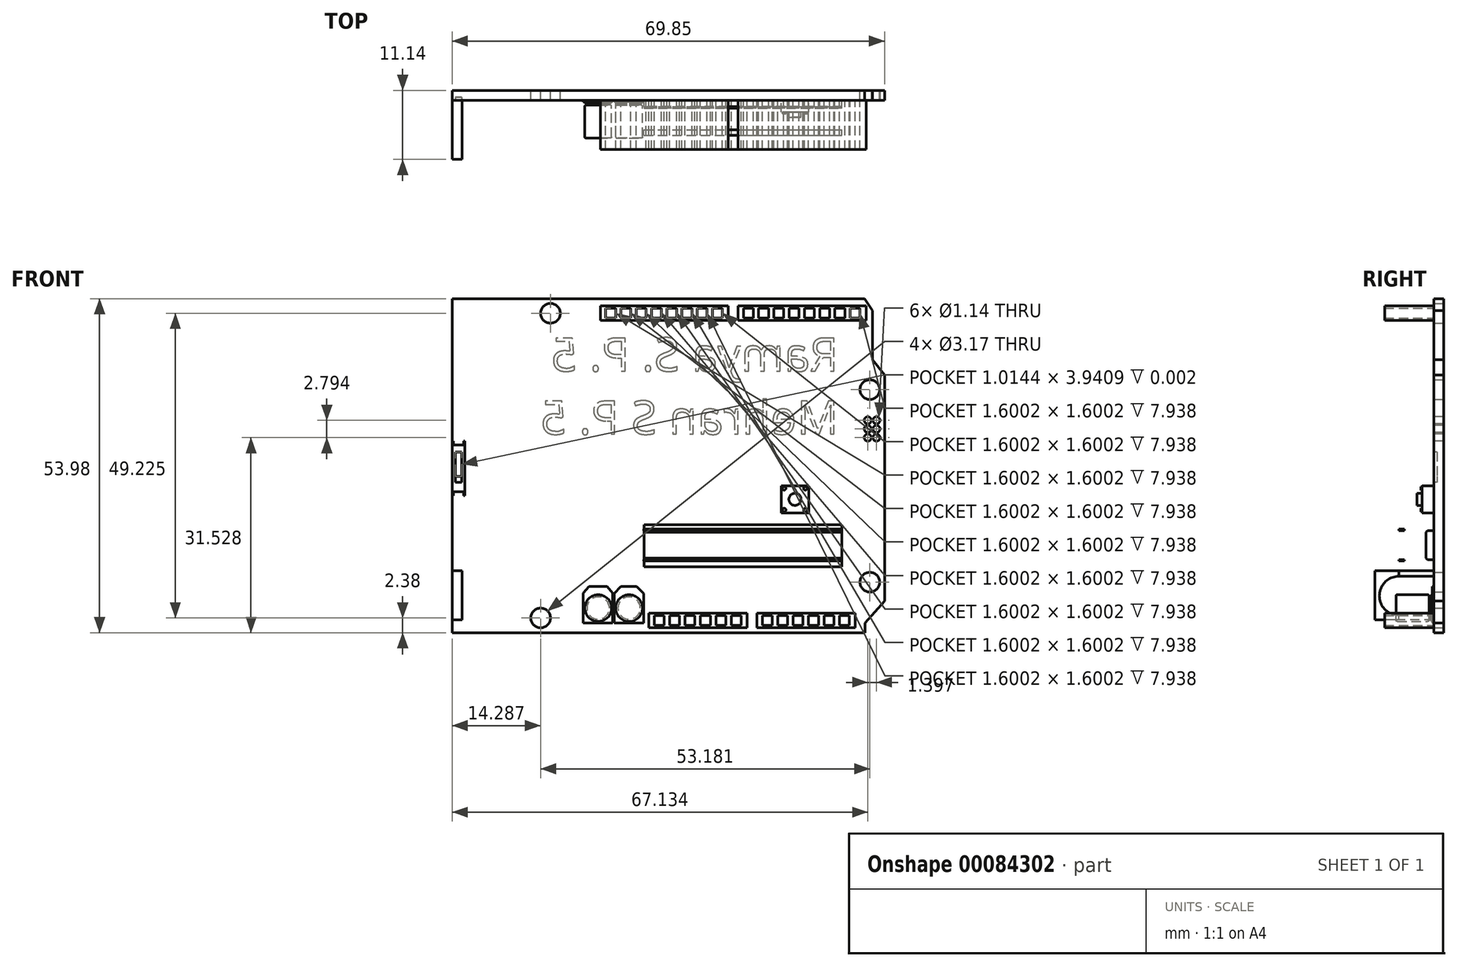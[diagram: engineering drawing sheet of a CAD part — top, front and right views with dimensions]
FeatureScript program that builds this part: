
annotation { "Feature Type Name" : "Feature", "Feature Type Description" : "" }
export const myFeature = defineFeature(function(context is Context, id is Id, definition is map)
    precondition{}
    {
        {
            var Q0;
            Q0=qCreatedBy(makeId("Front.planeOp"),FACE);
            var sketch = newSketch(context, id + "F0", { "sketchPlane" : qUnion([Q0])});
            skLineSegment(sketch, "E0.bottom", {"start": v(0, 0) * mm, "end": v(69.85, 0) * mm});
            skLineSegment(sketch, "E0.top", {"start": v(0, -53.97) * mm, "end": v(69.85, -53.97) * mm});
            skLineSegment(sketch, "E0.left", {"start": v(0, 0) * mm, "end": v(0, -53.97) * mm});
            skLineSegment(sketch, "E0.right", {"start": v(69.85, 0) * mm, "end": v(69.85, -53.97) * mm});
            skLineSegment(sketch, "E1", {"start": v(66.68, -53.97) * mm, "end": v(66.68, -52.39) * mm});
            skLineSegment(sketch, "E2", {"start": v(66.68, -52.39) * mm, "end": v(69.85, -48.84) * mm});
            skLineSegment(sketch, "E3", {"start": v(69.85, -12.33) * mm, "end": v(67.87, -9.84) * mm});
            skLineSegment(sketch, "E4", {"start": v(67.87, -9.84) * mm, "end": v(67.87, -1.9) * mm});
            skLineSegment(sketch, "E5", {"start": v(67.87, -1.9) * mm, "end": v(66.6, 0) * mm});
            skCircle(sketch, "E6", {"center": v(67.47, -14.7) * mm, "radius": 1.59 * mm});
            skCircle(sketch, "E7", {"center": v(67.47, -45.82) * mm, "radius": 1.59 * mm});
            skCircle(sketch, "E8", {"center": v(15.88, -2.37) * mm, "radius": 1.59 * mm});
            skCircle(sketch, "E9", {"center": v(14.29, -51.6) * mm, "radius": 1.59 * mm});
            skSolve(sketch);
        }
        {
            var Q0;
            {var subQ3=sQuery(id+"F0.wireOp",EDGE,"E0.left");Q0=makeQuery(id+"F0.imprint","IMPRINT",FACE,{"disambiguationData":[TD([[makeQuery(id+"F0.imprint","IMPRINT",EDGE,{"derivedFrom":subQ3}),1.0]])]});}
            extrude(context, id + "F1", {"entities" : qUnion([Q0]), "depth" : 1.59 * mm});
        }
        {
            var Q0;
            Q0=makeQuery(id+"F1.opExtrude","CAP_FACE",FACE,{"disambiguationData":[OSD([sQuery(id+"F0.wireOp",EDGE,"E0.bottom"),sQuery(id+"F0.wireOp",EDGE,"E0.top"),sQuery(id+"F0.wireOp",EDGE,"E0.left"),sQuery(id+"F0.wireOp",EDGE,"E0.right"),sQuery(id+"F0.wireOp",EDGE,"E1"),sQuery(id+"F0.wireOp",EDGE,"E2"),sQuery(id+"F0.wireOp",EDGE,"E3"),sQuery(id+"F0.wireOp",EDGE,"E4"),sQuery(id+"F0.wireOp",EDGE,"E5"),sQuery(id+"F0.wireOp",EDGE,"E6"),sQuery(id+"F0.wireOp",EDGE,"E7"),sQuery(id+"F0.wireOp",EDGE,"E8"),sQuery(id+"F0.wireOp",EDGE,"E9")])],"isStart":false});
            var sketch = newSketch(context, id + "F2", { "sketchPlane" : qUnion([Q0])});
            skLineSegment(sketch, "E10.bottom", {"start": v(65.09, -53.19) * mm, "end": v(49.21, -53.19) * mm});
            skLineSegment(sketch, "E10.top", {"start": v(65.09, -50.81) * mm, "end": v(49.21, -50.81) * mm});
            skLineSegment(sketch, "E10.left", {"start": v(65.09, -53.19) * mm, "end": v(65.09, -50.81) * mm});
            skLineSegment(sketch, "E10.right", {"start": v(49.21, -53.19) * mm, "end": v(49.21, -50.81) * mm});
            skLineSegment(sketch, "E11.bottom", {"start": v(47.63, -53.19) * mm, "end": v(31.75, -53.19) * mm});
            skLineSegment(sketch, "E11.top", {"start": v(47.63, -50.8) * mm, "end": v(31.75, -50.8) * mm});
            skLineSegment(sketch, "E11.left", {"start": v(47.63, -53.19) * mm, "end": v(47.63, -50.8) * mm});
            skLineSegment(sketch, "E11.right", {"start": v(31.75, -53.19) * mm, "end": v(31.75, -50.8) * mm});
            skLineSegment(sketch, "E12.bottom", {"start": v(46.2, -1.14) * mm, "end": v(66.86, -1.14) * mm});
            skLineSegment(sketch, "E12.top", {"start": v(46.2, -3.52) * mm, "end": v(66.86, -3.52) * mm});
            skLineSegment(sketch, "E12.left", {"start": v(46.2, -1.14) * mm, "end": v(46.2, -3.52) * mm});
            skLineSegment(sketch, "E12.right", {"start": v(66.86, -1.14) * mm, "end": v(66.86, -3.52) * mm});
            skLineSegment(sketch, "E13.bottom", {"start": v(44.62, -1.14) * mm, "end": v(23.97, -1.14) * mm});
            skLineSegment(sketch, "E13.top", {"start": v(44.62, -3.52) * mm, "end": v(23.97, -3.52) * mm});
            skLineSegment(sketch, "E13.left", {"start": v(44.62, -1.14) * mm, "end": v(44.62, -3.52) * mm});
            skLineSegment(sketch, "E13.right", {"start": v(23.97, -1.14) * mm, "end": v(23.97, -3.52) * mm});
            skLineSegment(sketch, "E14.bottom", {"start": v(24.8, -1.54) * mm, "end": v(26.4, -1.54) * mm});
            skLineSegment(sketch, "E14.top", {"start": v(24.8, -3.14) * mm, "end": v(26.4, -3.14) * mm});
            skLineSegment(sketch, "E14.left", {"start": v(24.8, -1.54) * mm, "end": v(24.8, -3.14) * mm});
            skLineSegment(sketch, "E14.right", {"start": v(26.4, -1.54) * mm, "end": v(26.4, -3.14) * mm});
            skLineSegment(sketch, "E15.bottom", {"start": v(27.27, -1.54) * mm, "end": v(28.87, -1.54) * mm});
            skLineSegment(sketch, "E15.top", {"start": v(27.27, -3.14) * mm, "end": v(28.87, -3.14) * mm});
            skLineSegment(sketch, "E15.left", {"start": v(27.27, -1.54) * mm, "end": v(27.27, -3.14) * mm});
            skLineSegment(sketch, "E15.right", {"start": v(28.87, -1.54) * mm, "end": v(28.87, -3.14) * mm});
            skLineSegment(sketch, "E16.bottom", {"start": v(29.73, -1.54) * mm, "end": v(31.33, -1.54) * mm});
            skLineSegment(sketch, "E16.top", {"start": v(29.73, -3.14) * mm, "end": v(31.33, -3.14) * mm});
            skLineSegment(sketch, "E16.left", {"start": v(29.73, -1.54) * mm, "end": v(29.73, -3.14) * mm});
            skLineSegment(sketch, "E16.right", {"start": v(31.33, -1.54) * mm, "end": v(31.33, -3.14) * mm});
            skLineSegment(sketch, "E17.bottom", {"start": v(32.2, -1.54) * mm, "end": v(33.8, -1.54) * mm});
            skLineSegment(sketch, "E17.top", {"start": v(32.2, -3.14) * mm, "end": v(33.8, -3.14) * mm});
            skLineSegment(sketch, "E17.left", {"start": v(32.2, -1.54) * mm, "end": v(32.2, -3.14) * mm});
            skLineSegment(sketch, "E17.right", {"start": v(33.8, -1.54) * mm, "end": v(33.8, -3.14) * mm});
            skLineSegment(sketch, "E18.bottom", {"start": v(34.66, -1.54) * mm, "end": v(36.26, -1.54) * mm});
            skLineSegment(sketch, "E18.top", {"start": v(34.66, -3.14) * mm, "end": v(36.26, -3.14) * mm});
            skLineSegment(sketch, "E18.left", {"start": v(34.66, -1.54) * mm, "end": v(34.66, -3.14) * mm});
            skLineSegment(sketch, "E18.right", {"start": v(36.26, -1.54) * mm, "end": v(36.26, -3.14) * mm});
            skLineSegment(sketch, "E19.bottom", {"start": v(37.12, -1.54) * mm, "end": v(38.72, -1.54) * mm});
            skLineSegment(sketch, "E19.top", {"start": v(37.12, -3.14) * mm, "end": v(38.72, -3.14) * mm});
            skLineSegment(sketch, "E19.left", {"start": v(37.12, -1.54) * mm, "end": v(37.12, -3.14) * mm});
            skLineSegment(sketch, "E19.right", {"start": v(38.72, -1.54) * mm, "end": v(38.72, -3.14) * mm});
            skLineSegment(sketch, "E20.bottom", {"start": v(39.59, -1.54) * mm, "end": v(41.19, -1.54) * mm});
            skLineSegment(sketch, "E20.top", {"start": v(39.59, -3.14) * mm, "end": v(41.19, -3.14) * mm});
            skLineSegment(sketch, "E20.left", {"start": v(39.59, -1.54) * mm, "end": v(39.59, -3.14) * mm});
            skLineSegment(sketch, "E20.right", {"start": v(41.19, -1.54) * mm, "end": v(41.19, -3.14) * mm});
            skLineSegment(sketch, "E21.bottom", {"start": v(42.05, -1.54) * mm, "end": v(43.65, -1.54) * mm});
            skLineSegment(sketch, "E21.top", {"start": v(42.05, -3.14) * mm, "end": v(43.65, -3.14) * mm});
            skLineSegment(sketch, "E21.left", {"start": v(42.05, -1.54) * mm, "end": v(42.05, -3.14) * mm});
            skLineSegment(sketch, "E21.right", {"start": v(43.65, -1.54) * mm, "end": v(43.65, -3.14) * mm});
            skLineSegment(sketch, "E22.bottom", {"start": v(47.04, -1.55) * mm, "end": v(48.64, -1.55) * mm});
            skLineSegment(sketch, "E22.top", {"start": v(47.04, -3.15) * mm, "end": v(48.64, -3.15) * mm});
            skLineSegment(sketch, "E22.left", {"start": v(47.04, -1.55) * mm, "end": v(47.04, -3.15) * mm});
            skLineSegment(sketch, "E22.right", {"start": v(48.64, -1.55) * mm, "end": v(48.64, -3.15) * mm});
            skPoint(sketch, "E23.firstSnap0", {"position": v(47.84, -1.55) * mm});
            skLineSegment(sketch, "E23.bottom", {"start": v(49.5, -1.55) * mm, "end": v(51.1, -1.55) * mm});
            skLineSegment(sketch, "E23.top", {"start": v(49.5, -3.15) * mm, "end": v(51.1, -3.15) * mm});
            skLineSegment(sketch, "E23.left", {"start": v(49.5, -1.55) * mm, "end": v(49.5, -3.15) * mm});
            skLineSegment(sketch, "E23.right", {"start": v(51.1, -1.55) * mm, "end": v(51.1, -3.15) * mm});
            skLineSegment(sketch, "E24.bottom", {"start": v(51.97, -1.55) * mm, "end": v(53.57, -1.55) * mm});
            skLineSegment(sketch, "E24.top", {"start": v(51.97, -3.15) * mm, "end": v(53.57, -3.15) * mm});
            skLineSegment(sketch, "E24.left", {"start": v(51.97, -1.55) * mm, "end": v(51.97, -3.15) * mm});
            skLineSegment(sketch, "E24.right", {"start": v(53.57, -1.55) * mm, "end": v(53.57, -3.15) * mm});
            skLineSegment(sketch, "E25.bottom", {"start": v(54.43, -1.55) * mm, "end": v(56.04, -1.55) * mm});
            skLineSegment(sketch, "E25.top", {"start": v(54.43, -3.15) * mm, "end": v(56.04, -3.15) * mm});
            skLineSegment(sketch, "E25.left", {"start": v(54.43, -1.55) * mm, "end": v(54.43, -3.15) * mm});
            skLineSegment(sketch, "E25.right", {"start": v(56.04, -1.55) * mm, "end": v(56.04, -3.15) * mm});
            skLineSegment(sketch, "E26.bottom", {"start": v(56.9, -1.55) * mm, "end": v(58.5, -1.55) * mm});
            skLineSegment(sketch, "E26.top", {"start": v(56.9, -3.15) * mm, "end": v(58.5, -3.15) * mm});
            skLineSegment(sketch, "E26.left", {"start": v(56.9, -1.55) * mm, "end": v(56.9, -3.15) * mm});
            skLineSegment(sketch, "E26.right", {"start": v(58.5, -1.55) * mm, "end": v(58.5, -3.15) * mm});
            skLineSegment(sketch, "E27.bottom", {"start": v(59.36, -1.55) * mm, "end": v(60.96, -1.55) * mm});
            skLineSegment(sketch, "E27.top", {"start": v(59.36, -3.15) * mm, "end": v(60.96, -3.15) * mm});
            skLineSegment(sketch, "E27.left", {"start": v(59.36, -1.55) * mm, "end": v(59.36, -3.15) * mm});
            skLineSegment(sketch, "E27.right", {"start": v(60.96, -1.55) * mm, "end": v(60.96, -3.15) * mm});
            skLineSegment(sketch, "E28.bottom", {"start": v(61.83, -1.55) * mm, "end": v(63.43, -1.55) * mm});
            skLineSegment(sketch, "E28.top", {"start": v(61.83, -3.15) * mm, "end": v(63.43, -3.15) * mm});
            skLineSegment(sketch, "E28.left", {"start": v(61.83, -1.55) * mm, "end": v(61.83, -3.15) * mm});
            skLineSegment(sketch, "E28.right", {"start": v(63.43, -1.55) * mm, "end": v(63.43, -3.15) * mm});
            skLineSegment(sketch, "E29.bottom", {"start": v(64.3, -1.55) * mm, "end": v(65.9, -1.55) * mm});
            skLineSegment(sketch, "E29.top", {"start": v(64.3, -3.15) * mm, "end": v(65.9, -3.15) * mm});
            skLineSegment(sketch, "E29.left", {"start": v(64.3, -1.55) * mm, "end": v(64.3, -3.15) * mm});
            skLineSegment(sketch, "E29.right", {"start": v(65.9, -1.55) * mm, "end": v(65.9, -3.15) * mm});
            skLineSegment(sketch, "E30.bottom", {"start": v(32.64, -51.2) * mm, "end": v(34.24, -51.2) * mm});
            skLineSegment(sketch, "E30.top", {"start": v(32.64, -52.8) * mm, "end": v(34.24, -52.8) * mm});
            skLineSegment(sketch, "E30.left", {"start": v(32.64, -51.2) * mm, "end": v(32.64, -52.8) * mm});
            skLineSegment(sketch, "E30.right", {"start": v(34.24, -51.2) * mm, "end": v(34.24, -52.8) * mm});
            skLineSegment(sketch, "E31.bottom", {"start": v(35.13, -51.2) * mm, "end": v(36.73, -51.2) * mm});
            skLineSegment(sketch, "E31.top", {"start": v(35.13, -52.8) * mm, "end": v(36.73, -52.8) * mm});
            skLineSegment(sketch, "E31.left", {"start": v(35.13, -51.2) * mm, "end": v(35.13, -52.8) * mm});
            skLineSegment(sketch, "E31.right", {"start": v(36.73, -51.2) * mm, "end": v(36.73, -52.8) * mm});
            skLineSegment(sketch, "E32.bottom", {"start": v(37.62, -51.2) * mm, "end": v(39.22, -51.2) * mm});
            skLineSegment(sketch, "E32.top", {"start": v(37.62, -52.8) * mm, "end": v(39.22, -52.8) * mm});
            skLineSegment(sketch, "E32.left", {"start": v(37.62, -51.2) * mm, "end": v(37.62, -52.8) * mm});
            skLineSegment(sketch, "E32.right", {"start": v(39.22, -51.2) * mm, "end": v(39.22, -52.8) * mm});
            skLineSegment(sketch, "E33.bottom", {"start": v(40.1, -51.2) * mm, "end": v(41.7, -51.2) * mm});
            skLineSegment(sketch, "E33.top", {"start": v(40.1, -52.8) * mm, "end": v(41.7, -52.8) * mm});
            skLineSegment(sketch, "E33.left", {"start": v(40.1, -51.2) * mm, "end": v(40.1, -52.8) * mm});
            skLineSegment(sketch, "E33.right", {"start": v(41.7, -51.2) * mm, "end": v(41.7, -52.8) * mm});
            skLineSegment(sketch, "E34.bottom", {"start": v(42.6, -51.2) * mm, "end": v(44.2, -51.2) * mm});
            skLineSegment(sketch, "E34.top", {"start": v(42.6, -52.8) * mm, "end": v(44.2, -52.8) * mm});
            skLineSegment(sketch, "E34.left", {"start": v(42.6, -51.2) * mm, "end": v(42.6, -52.8) * mm});
            skLineSegment(sketch, "E34.right", {"start": v(44.2, -51.2) * mm, "end": v(44.2, -52.8) * mm});
            skLineSegment(sketch, "E35.bottom", {"start": v(45.09, -51.2) * mm, "end": v(46.69, -51.2) * mm});
            skLineSegment(sketch, "E35.top", {"start": v(45.09, -52.8) * mm, "end": v(46.69, -52.8) * mm});
            skLineSegment(sketch, "E35.left", {"start": v(45.09, -51.2) * mm, "end": v(45.09, -52.8) * mm});
            skLineSegment(sketch, "E35.right", {"start": v(46.69, -51.2) * mm, "end": v(46.69, -52.8) * mm});
            skLineSegment(sketch, "E36.bottom", {"start": v(50.1, -51.22) * mm, "end": v(51.7, -51.22) * mm});
            skLineSegment(sketch, "E36.top", {"start": v(50.1, -52.82) * mm, "end": v(51.7, -52.82) * mm});
            skLineSegment(sketch, "E36.left", {"start": v(50.1, -51.22) * mm, "end": v(50.1, -52.82) * mm});
            skLineSegment(sketch, "E36.right", {"start": v(51.7, -51.22) * mm, "end": v(51.7, -52.82) * mm});
            skLineSegment(sketch, "E37.bottom", {"start": v(52.6, -51.22) * mm, "end": v(54.2, -51.22) * mm});
            skLineSegment(sketch, "E37.top", {"start": v(52.6, -52.82) * mm, "end": v(54.2, -52.82) * mm});
            skLineSegment(sketch, "E37.left", {"start": v(52.6, -51.22) * mm, "end": v(52.6, -52.82) * mm});
            skLineSegment(sketch, "E37.right", {"start": v(54.2, -51.22) * mm, "end": v(54.2, -52.82) * mm});
            skLineSegment(sketch, "E38.bottom", {"start": v(55.08, -51.22) * mm, "end": v(56.68, -51.22) * mm});
            skLineSegment(sketch, "E38.top", {"start": v(55.08, -52.82) * mm, "end": v(56.68, -52.82) * mm});
            skLineSegment(sketch, "E38.left", {"start": v(55.08, -51.22) * mm, "end": v(55.08, -52.82) * mm});
            skLineSegment(sketch, "E38.right", {"start": v(56.68, -51.22) * mm, "end": v(56.68, -52.82) * mm});
            skLineSegment(sketch, "E39.bottom", {"start": v(57.57, -51.22) * mm, "end": v(59.17, -51.22) * mm});
            skLineSegment(sketch, "E39.top", {"start": v(57.57, -52.82) * mm, "end": v(59.17, -52.82) * mm});
            skLineSegment(sketch, "E39.left", {"start": v(57.57, -51.22) * mm, "end": v(57.57, -52.82) * mm});
            skLineSegment(sketch, "E39.right", {"start": v(59.17, -51.22) * mm, "end": v(59.17, -52.82) * mm});
            skLineSegment(sketch, "E40.bottom", {"start": v(60.06, -51.22) * mm, "end": v(61.66, -51.22) * mm});
            skLineSegment(sketch, "E40.top", {"start": v(60.06, -52.82) * mm, "end": v(61.66, -52.82) * mm});
            skLineSegment(sketch, "E40.left", {"start": v(60.06, -51.22) * mm, "end": v(60.06, -52.82) * mm});
            skLineSegment(sketch, "E40.right", {"start": v(61.66, -51.22) * mm, "end": v(61.66, -52.82) * mm});
            skLineSegment(sketch, "E41.bottom", {"start": v(62.55, -51.22) * mm, "end": v(64.15, -51.22) * mm});
            skLineSegment(sketch, "E41.top", {"start": v(62.55, -52.82) * mm, "end": v(64.15, -52.82) * mm});
            skLineSegment(sketch, "E41.left", {"start": v(62.55, -51.22) * mm, "end": v(62.55, -52.82) * mm});
            skLineSegment(sketch, "E41.right", {"start": v(64.15, -51.22) * mm, "end": v(64.15, -52.82) * mm});
            skSolve(sketch);
        }
        {
            var Q0;
            Q0 = qSketchRegion(id + "F2", true);
            extrude(context, id + "F3", {"entities" : qUnion([Q0]), "operationType" : NewBodyOperationType.ADD, "depth" : 7.94 * mm});
        }
        {
            var Q0;
            Q0=makeQuery(id+"F1.opExtrude","CAP_FACE",FACE,{"disambiguationData":[OSD([sQuery(id+"F0.wireOp",EDGE,"E0.bottom"),sQuery(id+"F0.wireOp",EDGE,"E0.top"),sQuery(id+"F0.wireOp",EDGE,"E0.left"),sQuery(id+"F0.wireOp",EDGE,"E0.right"),sQuery(id+"F0.wireOp",EDGE,"E1"),sQuery(id+"F0.wireOp",EDGE,"E2"),sQuery(id+"F0.wireOp",EDGE,"E3"),sQuery(id+"F0.wireOp",EDGE,"E4"),sQuery(id+"F0.wireOp",EDGE,"E5"),sQuery(id+"F0.wireOp",EDGE,"E6"),sQuery(id+"F0.wireOp",EDGE,"E7"),sQuery(id+"F0.wireOp",EDGE,"E8"),sQuery(id+"F0.wireOp",EDGE,"E9")])],"isStart":true});
            var sketch = newSketch(context, id + "F4", { "sketchPlane" : qUnion([Q0])});
            skText(sketch, "E42", { "text": "Ramya S. P. 5\nMehran S P. 5", "fontName": "OpenSans-Regular.ttf"});
            const initialGuessF4  = {"E42": [-0.06243, -0.0117, 1, 0, 0.0054]};
            skSetInitialGuess(sketch, initialGuessF4);
            skSolve(sketch);
        }
        {
            var Q0;
            Q0 = qSketchRegion(id + "F4", true);
            extrude(context, id + "F5", {"entities" : qUnion([Q0]), "operationType" : NewBodyOperationType.ADD, "depth" : 0.03 * mm});
        }
        {
            var Q0;
            {var subQ0=sQuery(id+"F0.wireOp",EDGE,"E0.left");var subQ1=sQuery(id+"F0.wireOp",EDGE,"E2");var subQ2=sQuery(id+"F0.wireOp",EDGE,"E0.top");var subQ3=sQuery(id+"F0.wireOp",EDGE,"E9");var subQ4=sQuery(id+"F0.wireOp",EDGE,"E8");var subQ5=sQuery(id+"F0.wireOp",EDGE,"E7");var subQ6=sQuery(id+"F0.wireOp",EDGE,"E0.right");var subQ7=sQuery(id+"F0.wireOp",EDGE,"E0.bottom");var subQ8=sQuery(id+"F0.wireOp",EDGE,"E5");var subQ9=sQuery(id+"F0.wireOp",EDGE,"E1");var subQ10=sQuery(id+"F0.wireOp",EDGE,"E3");var subQ11=sQuery(id+"F0.wireOp",EDGE,"E4");var subQ12=sQuery(id+"F0.wireOp",EDGE,"E6");Q0=makeQuery(id+"F3.boolean.opBoolean","SPLIT",FACE,{"disambiguationData":[TD([makeQuery(id+"F1.opExtrude","SWEPT_FACE",FACE,{"disambiguationData":[OSD([subQ7])]})])],"derivedFrom":makeQuery(id+"F1.opExtrude","CAP_FACE",FACE,{"disambiguationData":[OSD([subQ7,subQ2,subQ0,subQ6,subQ9,subQ1,subQ10,subQ11,subQ8,subQ12,subQ5,subQ4,subQ3])],"isStart":false})});}
            var sketch = newSketch(context, id + "F6", { "sketchPlane" : qUnion([Q0])});
            skLineSegment(sketch, "E43.bottom", {"start": v(62.97, -43.34) * mm, "end": v(30.97, -43.34) * mm});
            skLineSegment(sketch, "E43.top", {"start": v(62.97, -36.52) * mm, "end": v(30.97, -36.52) * mm});
            skLineSegment(sketch, "E43.left", {"start": v(62.97, -43.34) * mm, "end": v(62.97, -36.52) * mm});
            skLineSegment(sketch, "E43.right", {"start": v(30.97, -43.34) * mm, "end": v(30.97, -36.52) * mm});
            skSolve(sketch);
        }
        {
            var Q0;
            Q0=makeQuery(id+"F6.imprint","IMPRINT",FACE,{"disambiguationData":[TD([[makeQuery(id+"F6.imprint","IMPRINT",EDGE,{"derivedFrom":sQuery(id+"F6.wireOp",EDGE,"E43.bottom")}),-1.0]])]});
            extrude(context, id + "F7", {"entities" : qUnion([Q0]), "operationType" : NewBodyOperationType.ADD, "depth" : 3 / 406.4 * mm});
        }
        {
            var Q0;
            Q0=makeQuery(id+"F7.opExtrude","CAP_FACE",FACE,{"disambiguationData":[OSD([sQuery(id+"F6.wireOp",EDGE,"E43.bottom"),sQuery(id+"F6.wireOp",EDGE,"E43.top"),sQuery(id+"F6.wireOp",EDGE,"E43.left"),sQuery(id+"F6.wireOp",EDGE,"E43.right")])],"isStart":false});
            var sketch = newSketch(context, id + "F8", { "sketchPlane" : qUnion([Q0])});
            skLineSegment(sketch, "E44.bottom", {"start": v(30.97, -37.48) * mm, "end": v(62.97, -37.48) * mm});
            skLineSegment(sketch, "E44.top", {"start": v(30.97, -42.17) * mm, "end": v(62.97, -42.17) * mm});
            skLineSegment(sketch, "E44.left", {"start": v(30.97, -37.48) * mm, "end": v(30.97, -42.17) * mm});
            skLineSegment(sketch, "E44.right", {"start": v(62.97, -37.48) * mm, "end": v(62.97, -42.17) * mm});
            skLineSegment(sketch, "E45.bottom", {"start": v(30.97, -42.17) * mm, "end": v(32.14, -42.17) * mm});
            skLineSegment(sketch, "E45.top", {"start": v(30.97, -37.48) * mm, "end": v(32.14, -37.48) * mm});
            skLineSegment(sketch, "E45.left", {"start": v(30.97, -42.17) * mm, "end": v(30.97, -37.48) * mm});
            skLineSegment(sketch, "E45.right", {"start": v(32.14, -42.17) * mm, "end": v(32.14, -37.48) * mm});
            skLineSegment(sketch, "E46.bottom", {"start": v(32.14, -42.17) * mm, "end": v(33.34, -42.17) * mm});
            skLineSegment(sketch, "E46.top", {"start": v(32.14, -37.48) * mm, "end": v(33.34, -37.48) * mm});
            skLineSegment(sketch, "E46.right", {"start": v(33.34, -42.17) * mm, "end": v(33.34, -37.48) * mm});
            skLineSegment(sketch, "E47.bottom", {"start": v(33.34, -42.17) * mm, "end": v(34.54, -42.17) * mm});
            skLineSegment(sketch, "E47.top", {"start": v(33.34, -37.48) * mm, "end": v(34.54, -37.48) * mm});
            skLineSegment(sketch, "E47.right", {"start": v(34.54, -42.17) * mm, "end": v(34.54, -37.48) * mm});
            skLineSegment(sketch, "E48.bottom", {"start": v(34.54, -42.17) * mm, "end": v(35.6, -42.17) * mm});
            skLineSegment(sketch, "E48.top", {"start": v(34.54, -37.48) * mm, "end": v(35.6, -37.48) * mm});
            skLineSegment(sketch, "E48.right", {"start": v(35.6, -42.17) * mm, "end": v(35.6, -37.48) * mm});
            skLineSegment(sketch, "E49.bottom", {"start": v(35.6, -42.17) * mm, "end": v(36.68, -42.17) * mm});
            skLineSegment(sketch, "E49.top", {"start": v(35.6, -37.48) * mm, "end": v(36.68, -37.48) * mm});
            skLineSegment(sketch, "E49.right", {"start": v(36.68, -42.17) * mm, "end": v(36.68, -37.48) * mm});
            skLineSegment(sketch, "E50.bottom", {"start": v(36.68, -42.17) * mm, "end": v(37.75, -42.17) * mm});
            skLineSegment(sketch, "E50.top", {"start": v(36.68, -37.48) * mm, "end": v(37.75, -37.48) * mm});
            skLineSegment(sketch, "E50.right", {"start": v(37.75, -42.17) * mm, "end": v(37.75, -37.48) * mm});
            skLineSegment(sketch, "E51.bottom", {"start": v(37.75, -42.17) * mm, "end": v(37.75, -42.17) * mm});
            skLineSegment(sketch, "E51.top", {"start": v(37.75, -37.48) * mm, "end": v(37.75, -37.48) * mm});
            skLineSegment(sketch, "E52.bottom", {"start": v(37.75, -42.17) * mm, "end": v(39.09, -42.17) * mm});
            skLineSegment(sketch, "E52.top", {"start": v(37.75, -37.48) * mm, "end": v(39.09, -37.48) * mm});
            skLineSegment(sketch, "E52.right", {"start": v(39.09, -42.17) * mm, "end": v(39.09, -37.48) * mm});
            skLineSegment(sketch, "E53.bottom", {"start": v(39.09, -42.17) * mm, "end": v(40.3, -42.17) * mm});
            skLineSegment(sketch, "E53.top", {"start": v(39.09, -37.48) * mm, "end": v(40.3, -37.48) * mm});
            skLineSegment(sketch, "E53.right", {"start": v(40.3, -42.17) * mm, "end": v(40.3, -37.48) * mm});
            skLineSegment(sketch, "E54.bottom", {"start": v(40.3, -42.17) * mm, "end": v(41.63, -42.17) * mm});
            skLineSegment(sketch, "E54.top", {"start": v(40.3, -37.48) * mm, "end": v(41.63, -37.48) * mm});
            skLineSegment(sketch, "E54.right", {"start": v(41.63, -42.17) * mm, "end": v(41.63, -37.48) * mm});
            skLineSegment(sketch, "E55.bottom", {"start": v(41.63, -42.17) * mm, "end": v(42.83, -42.17) * mm});
            skLineSegment(sketch, "E55.top", {"start": v(41.63, -37.48) * mm, "end": v(42.83, -37.48) * mm});
            skLineSegment(sketch, "E55.right", {"start": v(42.83, -42.17) * mm, "end": v(42.83, -37.48) * mm});
            skLineSegment(sketch, "E56.bottom", {"start": v(42.83, -42.17) * mm, "end": v(44.04, -42.17) * mm});
            skLineSegment(sketch, "E56.top", {"start": v(42.83, -37.48) * mm, "end": v(44.04, -37.48) * mm});
            skLineSegment(sketch, "E56.right", {"start": v(44.04, -42.17) * mm, "end": v(44.04, -37.48) * mm});
            skLineSegment(sketch, "E57.bottom", {"start": v(44.04, -42.17) * mm, "end": v(45.23, -42.17) * mm});
            skLineSegment(sketch, "E57.top", {"start": v(44.04, -37.48) * mm, "end": v(45.23, -37.48) * mm});
            skLineSegment(sketch, "E57.right", {"start": v(45.23, -42.17) * mm, "end": v(45.23, -37.48) * mm});
            skLineSegment(sketch, "E58.bottom", {"start": v(45.23, -42.17) * mm, "end": v(45.23, -42.17) * mm});
            skLineSegment(sketch, "E58.top", {"start": v(45.23, -37.48) * mm, "end": v(45.23, -37.48) * mm});
            skLineSegment(sketch, "E59.bottom", {"start": v(45.23, -42.17) * mm, "end": v(46.97, -42.17) * mm});
            skLineSegment(sketch, "E59.top", {"start": v(45.23, -37.48) * mm, "end": v(46.97, -37.48) * mm});
            skLineSegment(sketch, "E59.right", {"start": v(46.97, -42.17) * mm, "end": v(46.97, -37.48) * mm});
            skLineSegment(sketch, "E60.bottom", {"start": v(46.97, -42.17) * mm, "end": v(48.18, -42.17) * mm});
            skLineSegment(sketch, "E60.top", {"start": v(46.97, -37.48) * mm, "end": v(48.18, -37.48) * mm});
            skLineSegment(sketch, "E60.right", {"start": v(48.18, -42.17) * mm, "end": v(48.18, -37.48) * mm});
            skLineSegment(sketch, "E61.bottom", {"start": v(48.18, -42.17) * mm, "end": v(49.26, -42.17) * mm});
            skLineSegment(sketch, "E61.top", {"start": v(48.18, -37.48) * mm, "end": v(49.26, -37.48) * mm});
            skLineSegment(sketch, "E61.right", {"start": v(49.26, -42.17) * mm, "end": v(49.26, -37.48) * mm});
            skLineSegment(sketch, "E62.bottom", {"start": v(49.26, -42.17) * mm, "end": v(50.32, -42.17) * mm});
            skLineSegment(sketch, "E62.top", {"start": v(49.26, -37.48) * mm, "end": v(50.32, -37.48) * mm});
            skLineSegment(sketch, "E62.right", {"start": v(50.32, -42.17) * mm, "end": v(50.32, -37.48) * mm});
            skLineSegment(sketch, "E63.bottom", {"start": v(50.32, -42.17) * mm, "end": v(51.53, -42.17) * mm});
            skLineSegment(sketch, "E63.top", {"start": v(50.32, -37.48) * mm, "end": v(51.53, -37.48) * mm});
            skLineSegment(sketch, "E63.right", {"start": v(51.53, -42.17) * mm, "end": v(51.53, -37.48) * mm});
            skLineSegment(sketch, "E64.bottom", {"start": v(51.53, -42.17) * mm, "end": v(52.73, -42.17) * mm});
            skLineSegment(sketch, "E64.top", {"start": v(51.53, -37.48) * mm, "end": v(52.73, -37.48) * mm});
            skLineSegment(sketch, "E64.right", {"start": v(52.73, -42.17) * mm, "end": v(52.73, -37.48) * mm});
            skLineSegment(sketch, "E65.bottom", {"start": v(52.73, -42.17) * mm, "end": v(53.94, -42.17) * mm});
            skLineSegment(sketch, "E65.top", {"start": v(52.73, -37.48) * mm, "end": v(53.94, -37.48) * mm});
            skLineSegment(sketch, "E65.right", {"start": v(53.94, -42.17) * mm, "end": v(53.94, -37.48) * mm});
            skLineSegment(sketch, "E66.bottom", {"start": v(53.94, -42.17) * mm, "end": v(55.08, -42.17) * mm});
            skLineSegment(sketch, "E66.top", {"start": v(53.94, -37.48) * mm, "end": v(55.08, -37.48) * mm});
            skLineSegment(sketch, "E66.right", {"start": v(55.08, -42.17) * mm, "end": v(55.08, -37.48) * mm});
            skLineSegment(sketch, "E67.bottom", {"start": v(55.08, -42.17) * mm, "end": v(56.24, -42.17) * mm});
            skLineSegment(sketch, "E67.top", {"start": v(55.08, -37.48) * mm, "end": v(56.24, -37.48) * mm});
            skLineSegment(sketch, "E67.right", {"start": v(56.24, -42.17) * mm, "end": v(56.24, -37.48) * mm});
            skLineSegment(sketch, "E68.bottom", {"start": v(56.24, -42.17) * mm, "end": v(57.4, -42.17) * mm});
            skLineSegment(sketch, "E68.top", {"start": v(56.24, -37.48) * mm, "end": v(57.4, -37.48) * mm});
            skLineSegment(sketch, "E68.right", {"start": v(57.4, -42.17) * mm, "end": v(57.4, -37.48) * mm});
            skLineSegment(sketch, "E69.bottom", {"start": v(57.4, -42.17) * mm, "end": v(58.46, -42.17) * mm});
            skLineSegment(sketch, "E69.top", {"start": v(57.4, -37.48) * mm, "end": v(58.46, -37.48) * mm});
            skLineSegment(sketch, "E69.right", {"start": v(58.46, -42.17) * mm, "end": v(58.46, -37.48) * mm});
            skLineSegment(sketch, "E70.bottom", {"start": v(58.46, -42.17) * mm, "end": v(59.52, -42.17) * mm});
            skLineSegment(sketch, "E70.top", {"start": v(58.46, -37.48) * mm, "end": v(59.52, -37.48) * mm});
            skLineSegment(sketch, "E70.right", {"start": v(59.52, -42.17) * mm, "end": v(59.52, -37.48) * mm});
            skLineSegment(sketch, "E71.bottom", {"start": v(59.52, -42.17) * mm, "end": v(60.47, -42.17) * mm});
            skLineSegment(sketch, "E71.top", {"start": v(59.52, -37.48) * mm, "end": v(60.47, -37.48) * mm});
            skLineSegment(sketch, "E71.right", {"start": v(60.47, -42.17) * mm, "end": v(60.47, -37.48) * mm});
            skLineSegment(sketch, "E72.bottom", {"start": v(60.47, -42.17) * mm, "end": v(61.52, -42.17) * mm});
            skLineSegment(sketch, "E72.top", {"start": v(60.47, -37.48) * mm, "end": v(61.52, -37.48) * mm});
            skLineSegment(sketch, "E72.right", {"start": v(61.52, -42.17) * mm, "end": v(61.52, -37.48) * mm});
            skSolve(sketch);
        }
        {
            var Q0;
            Q0=makeQuery(id+"F8.imprint","IMPRINT",FACE,{"disambiguationData":[TD([[makeQuery(id+"F8.imprint","IMPRINT",EDGE,{"derivedFrom":sQuery(id+"F8.wireOp",EDGE,"E44.bottom")}),-1.0]])]});
            var Q1;
            Q1=makeQuery(id+"F8.imprint","IMPRINT",FACE,{"disambiguationData":[TD([[makeQuery(id+"F8.imprint","IMPRINT",EDGE,{"derivedFrom":sQuery(id+"F8.wireOp",EDGE,"E72.bottom")}),1.0]])]});
            var Q2;
            Q2=makeQuery(id+"F8.imprint","IMPRINT",FACE,{"disambiguationData":[TD([[makeQuery(id+"F8.imprint","IMPRINT",EDGE,{"derivedFrom":sQuery(id+"F8.wireOp",EDGE,"E71.bottom")}),1.0]])]});
            var Q3;
            Q3=makeQuery(id+"F8.imprint","IMPRINT",FACE,{"disambiguationData":[TD([[makeQuery(id+"F8.imprint","IMPRINT",EDGE,{"derivedFrom":sQuery(id+"F8.wireOp",EDGE,"E70.bottom")}),1.0]])]});
            var Q4;
            Q4=makeQuery(id+"F8.imprint","IMPRINT",FACE,{"disambiguationData":[TD([[makeQuery(id+"F8.imprint","IMPRINT",EDGE,{"derivedFrom":sQuery(id+"F8.wireOp",EDGE,"E69.bottom")}),1.0]])]});
            var Q5;
            Q5=makeQuery(id+"F8.imprint","IMPRINT",FACE,{"disambiguationData":[TD([[makeQuery(id+"F8.imprint","IMPRINT",EDGE,{"derivedFrom":sQuery(id+"F8.wireOp",EDGE,"E68.bottom")}),1.0]])]});
            var Q6;
            Q6=makeQuery(id+"F8.imprint","IMPRINT",FACE,{"disambiguationData":[TD([[makeQuery(id+"F8.imprint","IMPRINT",EDGE,{"derivedFrom":sQuery(id+"F8.wireOp",EDGE,"E67.bottom")}),1.0]])]});
            var Q7;
            Q7=makeQuery(id+"F8.imprint","IMPRINT",FACE,{"disambiguationData":[TD([[makeQuery(id+"F8.imprint","IMPRINT",EDGE,{"derivedFrom":sQuery(id+"F8.wireOp",EDGE,"E66.bottom")}),1.0]])]});
            var Q8;
            Q8=makeQuery(id+"F8.imprint","IMPRINT",FACE,{"disambiguationData":[TD([[makeQuery(id+"F8.imprint","IMPRINT",EDGE,{"derivedFrom":sQuery(id+"F8.wireOp",EDGE,"E65.bottom")}),1.0]])]});
            var Q9;
            Q9=makeQuery(id+"F8.imprint","IMPRINT",FACE,{"disambiguationData":[TD([[makeQuery(id+"F8.imprint","IMPRINT",EDGE,{"derivedFrom":sQuery(id+"F8.wireOp",EDGE,"E64.bottom")}),1.0]])]});
            var Q10;
            Q10=makeQuery(id+"F8.imprint","IMPRINT",FACE,{"disambiguationData":[TD([[makeQuery(id+"F8.imprint","IMPRINT",EDGE,{"derivedFrom":sQuery(id+"F8.wireOp",EDGE,"E63.bottom")}),1.0]])]});
            var Q11;
            Q11=makeQuery(id+"F8.imprint","IMPRINT",FACE,{"disambiguationData":[TD([[makeQuery(id+"F8.imprint","IMPRINT",EDGE,{"derivedFrom":sQuery(id+"F8.wireOp",EDGE,"E62.bottom")}),1.0]])]});
            var Q12;
            Q12=makeQuery(id+"F8.imprint","IMPRINT",FACE,{"disambiguationData":[TD([[makeQuery(id+"F8.imprint","IMPRINT",EDGE,{"derivedFrom":sQuery(id+"F8.wireOp",EDGE,"E61.bottom")}),1.0]])]});
            var Q13;
            Q13=makeQuery(id+"F8.imprint","IMPRINT",FACE,{"disambiguationData":[TD([[makeQuery(id+"F8.imprint","IMPRINT",EDGE,{"derivedFrom":sQuery(id+"F8.wireOp",EDGE,"E60.bottom")}),1.0]])]});
            var Q14;
            Q14=makeQuery(id+"F8.imprint","IMPRINT",FACE,{"disambiguationData":[TD([[makeQuery(id+"F8.imprint","IMPRINT",EDGE,{"derivedFrom":sQuery(id+"F8.wireOp",EDGE,"E59.bottom")}),1.0]])]});
            var Q15;
            Q15=makeQuery(id+"F8.imprint","IMPRINT",FACE,{"disambiguationData":[TD([[makeQuery(id+"F8.imprint","IMPRINT",EDGE,{"derivedFrom":sQuery(id+"F8.wireOp",EDGE,"E57.bottom")}),1.0]])]});
            var Q16;
            Q16=makeQuery(id+"F8.imprint","IMPRINT",FACE,{"disambiguationData":[TD([[makeQuery(id+"F8.imprint","IMPRINT",EDGE,{"derivedFrom":sQuery(id+"F8.wireOp",EDGE,"E56.bottom")}),1.0]])]});
            var Q17;
            Q17=makeQuery(id+"F8.imprint","IMPRINT",FACE,{"disambiguationData":[TD([[makeQuery(id+"F8.imprint","IMPRINT",EDGE,{"derivedFrom":sQuery(id+"F8.wireOp",EDGE,"E55.bottom")}),1.0]])]});
            var Q18;
            Q18=makeQuery(id+"F8.imprint","IMPRINT",FACE,{"disambiguationData":[TD([[makeQuery(id+"F8.imprint","IMPRINT",EDGE,{"derivedFrom":sQuery(id+"F8.wireOp",EDGE,"E54.bottom")}),1.0]])]});
            var Q19;
            Q19=makeQuery(id+"F8.imprint","IMPRINT",FACE,{"disambiguationData":[TD([[makeQuery(id+"F8.imprint","IMPRINT",EDGE,{"derivedFrom":sQuery(id+"F8.wireOp",EDGE,"E53.bottom")}),1.0]])]});
            var Q20;
            Q20=makeQuery(id+"F8.imprint","IMPRINT",FACE,{"disambiguationData":[TD([[makeQuery(id+"F8.imprint","IMPRINT",EDGE,{"derivedFrom":sQuery(id+"F8.wireOp",EDGE,"E52.bottom")}),1.0]])]});
            var Q21;
            Q21=makeQuery(id+"F8.imprint","IMPRINT",FACE,{"disambiguationData":[TD([[makeQuery(id+"F8.imprint","IMPRINT",EDGE,{"derivedFrom":sQuery(id+"F8.wireOp",EDGE,"E50.bottom")}),1.0]])]});
            var Q22;
            Q22=makeQuery(id+"F8.imprint","IMPRINT",FACE,{"disambiguationData":[TD([[makeQuery(id+"F8.imprint","IMPRINT",EDGE,{"derivedFrom":sQuery(id+"F8.wireOp",EDGE,"E49.bottom")}),1.0]])]});
            var Q23;
            Q23=makeQuery(id+"F8.imprint","IMPRINT",FACE,{"disambiguationData":[TD([[makeQuery(id+"F8.imprint","IMPRINT",EDGE,{"derivedFrom":sQuery(id+"F8.wireOp",EDGE,"E48.bottom")}),1.0]])]});
            var Q24;
            Q24=makeQuery(id+"F8.imprint","IMPRINT",FACE,{"disambiguationData":[TD([[makeQuery(id+"F8.imprint","IMPRINT",EDGE,{"derivedFrom":sQuery(id+"F8.wireOp",EDGE,"E47.bottom")}),1.0]])]});
            var Q25;
            Q25=makeQuery(id+"F8.imprint","IMPRINT",FACE,{"disambiguationData":[TD([[makeQuery(id+"F8.imprint","IMPRINT",EDGE,{"derivedFrom":sQuery(id+"F8.wireOp",EDGE,"E46.bottom")}),1.0]])]});
            var Q26;
            Q26=makeQuery(id+"F8.imprint","IMPRINT",FACE,{"disambiguationData":[TD([[makeQuery(id+"F8.imprint","IMPRINT",EDGE,{"derivedFrom":sQuery(id+"F8.wireOp",EDGE,"E45.bottom")}),1.0]])]});
            extrude(context, id + "F9", {"entities" : qUnion([Q0, Q1, Q2, Q3, Q4, Q5, Q6, Q7, Q8, Q9, Q10, Q11, Q12, Q13, Q14, Q15, Q16, Q17, Q18, Q19, Q20, Q21, Q22, Q23, Q24, Q25, Q26]), "operationType" : NewBodyOperationType.ADD, "depth" : 1.27 * mm});
        }
        {
            var Q0;
            Q0=makeQuery(id+"F9.opExtrude","CAP_EDGE",EDGE,{"disambiguationData":[OSD([sQuery(id+"F8.wireOp",EDGE,"E44.top")])],"isStart":false});
            var Q1;
            Q1=makeQuery(id+"F9.opExtrude","CAP_EDGE",EDGE,{"disambiguationData":[OSD([sQuery(id+"F8.wireOp",EDGE,"E44.bottom")])],"isStart":false});
            chamfer(context, id + "F10", {"entities" : qUnion([Q0, Q1]), "width" : 0.25 * mm, "tangentPropagation" : true});
        }
        {
            var Q0;
            Q0=makeQuery(id+"F9.boolean.opBoolean","MERGE",FACE,{"derivedFrom":[makeQuery(id+"F7.opExtrude","SWEPT_FACE",FACE,{"disambiguationData":[OSD([sQuery(id+"F6.wireOp",EDGE,"E43.left")])]}),makeQuery(id+"F9.opExtrude","SWEPT_FACE",FACE,{"disambiguationData":[OSD([sQuery(id+"F8.wireOp",EDGE,"E44.right")])]})]});
            var sketch = newSketch(context, id + "F11", { "sketchPlane" : qUnion([Q0])});
            skLineSegment(sketch, "E73.bottom", {"start": v(-7.37, -42.17) * mm, "end": v(-6.35, -42.17) * mm});
            skLineSegment(sketch, "E73.top", {"start": v(-7.37, -42.5) * mm, "end": v(-6.35, -42.5) * mm});
            skLineSegment(sketch, "E73.left", {"start": v(-7.37, -42.17) * mm, "end": v(-7.37, -42.5) * mm});
            skLineSegment(sketch, "E73.right", {"start": v(-6.35, -42.17) * mm, "end": v(-6.35, -42.5) * mm});
            skLineSegment(sketch, "E74.bottom", {"start": v(-7.22, -42.17) * mm, "end": v(-6.35, -42.17) * mm});
            skLineSegment(sketch, "E74.top", {"start": v(-7.22, -42.38) * mm, "end": v(-6.35, -42.38) * mm});
            skLineSegment(sketch, "E74.left", {"start": v(-7.22, -42.17) * mm, "end": v(-7.22, -42.38) * mm});
            skLineSegment(sketch, "E74.right", {"start": v(-6.35, -42.17) * mm, "end": v(-6.35, -42.38) * mm});
            skLineSegment(sketch, "E75.bottom", {"start": v(-7.37, -37.48) * mm, "end": v(-6.35, -37.48) * mm});
            skLineSegment(sketch, "E75.top", {"start": v(-7.37, -37.15) * mm, "end": v(-6.35, -37.15) * mm});
            skLineSegment(sketch, "E75.left", {"start": v(-7.37, -37.48) * mm, "end": v(-7.37, -37.15) * mm});
            skLineSegment(sketch, "E75.right", {"start": v(-6.35, -37.48) * mm, "end": v(-6.35, -37.15) * mm});
            skLineSegment(sketch, "E76.bottom", {"start": v(-7.22, -37.48) * mm, "end": v(-6.35, -37.48) * mm});
            skLineSegment(sketch, "E76.top", {"start": v(-7.22, -37.27) * mm, "end": v(-6.35, -37.27) * mm});
            skLineSegment(sketch, "E76.left", {"start": v(-7.22, -37.48) * mm, "end": v(-7.22, -37.27) * mm});
            skLineSegment(sketch, "E76.right", {"start": v(-6.35, -37.48) * mm, "end": v(-6.35, -37.27) * mm});
            skSolve(sketch);
        }
        {
            var Q0;
            Q0=makeQuery(id+"F11.imprint","IMPRINT",FACE,{"disambiguationData":[TD([[makeQuery(id+"F11.imprint","IMPRINT",EDGE,{"derivedFrom":sQuery(id+"F11.wireOp",EDGE,"E73.bottom")}),-1.0]])]});
            var Q1;
            Q1=makeQuery(id+"F11.imprint","IMPRINT",FACE,{"disambiguationData":[TD([[makeQuery(id+"F11.imprint","IMPRINT",EDGE,{"derivedFrom":sQuery(id+"F11.wireOp",EDGE,"E75.bottom")}),1.0]])]});
            extrude(context, id + "F12", {"entities" : qUnion([Q0, Q1]), "operationType" : NewBodyOperationType.ADD, "oppositeDirection" : true, "depth" : 32 * mm});
        }
        {
            var Q0;
            {var subQ0=sQuery(id+"F0.wireOp",EDGE,"E0.left");var subQ1=sQuery(id+"F0.wireOp",EDGE,"E2");var subQ2=sQuery(id+"F0.wireOp",EDGE,"E0.top");var subQ3=sQuery(id+"F0.wireOp",EDGE,"E9");var subQ4=sQuery(id+"F0.wireOp",EDGE,"E8");var subQ5=sQuery(id+"F0.wireOp",EDGE,"E7");var subQ6=sQuery(id+"F0.wireOp",EDGE,"E0.right");var subQ7=sQuery(id+"F0.wireOp",EDGE,"E0.bottom");var subQ8=sQuery(id+"F0.wireOp",EDGE,"E5");var subQ9=sQuery(id+"F0.wireOp",EDGE,"E1");var subQ10=sQuery(id+"F0.wireOp",EDGE,"E3");var subQ11=sQuery(id+"F0.wireOp",EDGE,"E4");var subQ12=sQuery(id+"F0.wireOp",EDGE,"E6");Q0=makeQuery(id+"F3.boolean.opBoolean","SPLIT",FACE,{"disambiguationData":[TD([makeQuery(id+"F1.opExtrude","SWEPT_FACE",FACE,{"disambiguationData":[OSD([subQ7])]})])],"derivedFrom":makeQuery(id+"F1.opExtrude","CAP_FACE",FACE,{"disambiguationData":[OSD([subQ7,subQ2,subQ0,subQ6,subQ9,subQ1,subQ10,subQ11,subQ8,subQ12,subQ5,subQ4,subQ3])],"isStart":false})});}
            var sketch = newSketch(context, id + "F13", { "sketchPlane" : qUnion([Q0])});
            skLineSegment(sketch, "E77.bottom", {"start": v(57.61, -34.63) * mm, "end": v(53.14, -34.63) * mm});
            skLineSegment(sketch, "E77.top", {"start": v(57.61, -30.23) * mm, "end": v(53.14, -30.23) * mm});
            skLineSegment(sketch, "E77.left", {"start": v(57.61, -34.63) * mm, "end": v(57.61, -30.23) * mm});
            skLineSegment(sketch, "E77.right", {"start": v(53.14, -34.63) * mm, "end": v(53.14, -30.23) * mm});
            skSolve(sketch);
        }
        {
            var Q0;
            Q0 = qSketchRegion(id + "F13", true);
            extrude(context, id + "F14", {"entities" : qUnion([Q0]), "operationType" : NewBodyOperationType.ADD, "depth" : 1.9 * mm});
        }
        {
            var Q0;
            Q0=makeQuery(id+"F14.opExtrude","CAP_FACE",FACE,{"disambiguationData":[OSD([sQuery(id+"F13.wireOp",EDGE,"E77.bottom"),sQuery(id+"F13.wireOp",EDGE,"E77.top"),sQuery(id+"F13.wireOp",EDGE,"E77.left"),sQuery(id+"F13.wireOp",EDGE,"E77.right")])],"isStart":false});
            var sketch = newSketch(context, id + "F15", { "sketchPlane" : qUnion([Q0])});
            skCircle(sketch, "E78", {"center": v(55.38, -32.43) * mm, "radius": 0.98 * mm});
            skPoint(sketch, "E78.centerSnap0", {"position": v(57.61, -32.43) * mm});
            skPoint(sketch, "E78.centerSnap1", {"position": v(55.38, -30.23) * mm});
            skSolve(sketch);
        }
        {
            var Q0;
            Q0 = qSketchRegion(id + "F15", true);
            extrude(context, id + "F16", {"entities" : qUnion([Q0]), "operationType" : NewBodyOperationType.ADD, "depth" : 0.8 * mm});
        }
        {
            var Q0;
            Q0=makeQuery(id+"F14.opExtrude","CAP_FACE",FACE,{"disambiguationData":[OSD([sQuery(id+"F13.wireOp",EDGE,"E77.bottom"),sQuery(id+"F13.wireOp",EDGE,"E77.top"),sQuery(id+"F13.wireOp",EDGE,"E77.left"),sQuery(id+"F13.wireOp",EDGE,"E77.right")])],"isStart":false});
            var sketch = newSketch(context, id + "F17", { "sketchPlane" : qUnion([Q0])});
            skCircle(sketch, "E79", {"center": v(53.62, -30.65) * mm, "radius": 0.3 * mm});
            skCircle(sketch, "E80", {"center": v(53.62, -34.14) * mm, "radius": 0.29 * mm});
            skCircle(sketch, "E81", {"center": v(57.05, -34.14) * mm, "radius": 0.29 * mm});
            skCircle(sketch, "E82", {"center": v(57.05, -30.65) * mm, "radius": 0.3 * mm});
            skSolve(sketch);
        }
        {
            var Q0;
            Q0=makeQuery(id+"F17.imprint","IMPRINT",FACE,{"disambiguationData":[TD([[makeQuery(id+"F17.imprint","IMPRINT",EDGE,{"derivedFrom":sQuery(id+"F17.wireOp",EDGE,"E80")}),1.0]])]});
            var Q1;
            Q1=makeQuery(id+"F17.imprint","IMPRINT",FACE,{"disambiguationData":[TD([[makeQuery(id+"F17.imprint","IMPRINT",EDGE,{"derivedFrom":sQuery(id+"F17.wireOp",EDGE,"E81")}),1.0]])]});
            var Q2;
            Q2=makeQuery(id+"F17.imprint","IMPRINT",FACE,{"disambiguationData":[TD([[makeQuery(id+"F17.imprint","IMPRINT",EDGE,{"derivedFrom":sQuery(id+"F17.wireOp",EDGE,"E82")}),1.0]])]});
            var Q3;
            Q3=makeQuery(id+"F17.imprint","IMPRINT",FACE,{"disambiguationData":[TD([[makeQuery(id+"F17.imprint","IMPRINT",EDGE,{"derivedFrom":sQuery(id+"F17.wireOp",EDGE,"E79")}),1.0]])]});
            extrude(context, id + "F18", {"entities" : qUnion([Q0, Q1, Q2, Q3]), "operationType" : NewBodyOperationType.ADD, "depth" : 0.2 * mm});
        }
        {
            var Q0;
            {var subQ0=sQuery(id+"F0.wireOp",EDGE,"E0.left");var subQ1=sQuery(id+"F0.wireOp",EDGE,"E2");var subQ2=sQuery(id+"F0.wireOp",EDGE,"E0.top");var subQ3=sQuery(id+"F0.wireOp",EDGE,"E9");var subQ4=sQuery(id+"F0.wireOp",EDGE,"E8");var subQ5=sQuery(id+"F0.wireOp",EDGE,"E7");var subQ6=sQuery(id+"F0.wireOp",EDGE,"E0.right");var subQ7=sQuery(id+"F0.wireOp",EDGE,"E0.bottom");var subQ8=sQuery(id+"F0.wireOp",EDGE,"E5");var subQ9=sQuery(id+"F0.wireOp",EDGE,"E1");var subQ10=sQuery(id+"F0.wireOp",EDGE,"E3");var subQ11=sQuery(id+"F0.wireOp",EDGE,"E4");var subQ12=sQuery(id+"F0.wireOp",EDGE,"E6");Q0=makeQuery(id+"F3.boolean.opBoolean","SPLIT",FACE,{"disambiguationData":[TD([makeQuery(id+"F1.opExtrude","SWEPT_FACE",FACE,{"disambiguationData":[OSD([subQ7])]})])],"derivedFrom":makeQuery(id+"F1.opExtrude","CAP_FACE",FACE,{"disambiguationData":[OSD([subQ7,subQ2,subQ0,subQ6,subQ9,subQ1,subQ10,subQ11,subQ8,subQ12,subQ5,subQ4,subQ3])],"isStart":false})});}
            var sketch = newSketch(context, id + "F19", { "sketchPlane" : qUnion([Q0])});
            skLineSegment(sketch, "E83.bottom", {"start": v(26.2, -47.62) * mm, "end": v(30.96, -47.62) * mm});
            skLineSegment(sketch, "E83.top", {"start": v(26.2, -52.39) * mm, "end": v(30.96, -52.39) * mm});
            skLineSegment(sketch, "E83.left", {"start": v(26.2, -47.62) * mm, "end": v(26.2, -52.39) * mm});
            skLineSegment(sketch, "E83.right", {"start": v(30.96, -47.62) * mm, "end": v(30.96, -52.39) * mm});
            skLineSegment(sketch, "E84.bottom", {"start": v(25.95, -52.39) * mm, "end": v(21.17, -52.39) * mm});
            skLineSegment(sketch, "E84.top", {"start": v(25.95, -47.61) * mm, "end": v(21.17, -47.61) * mm});
            skLineSegment(sketch, "E84.left", {"start": v(25.95, -52.39) * mm, "end": v(25.95, -47.61) * mm});
            skLineSegment(sketch, "E84.right", {"start": v(21.17, -52.39) * mm, "end": v(21.17, -47.61) * mm});
            skLineSegment(sketch, "E85.bottom", {"start": v(22.12, -47.61) * mm, "end": v(25.05, -47.61) * mm});
            skLineSegment(sketch, "E85.top", {"start": v(22.12, -46.53) * mm, "end": v(25.05, -46.53) * mm});
            skLineSegment(sketch, "E85.left", {"start": v(22.12, -47.61) * mm, "end": v(22.12, -46.53) * mm});
            skLineSegment(sketch, "E85.right", {"start": v(25.05, -47.61) * mm, "end": v(25.05, -46.53) * mm});
            skLineSegment(sketch, "E86", {"start": v(21.17, -47.61) * mm, "end": v(22.12, -46.53) * mm});
            skLineSegment(sketch, "E87", {"start": v(25.05, -46.53) * mm, "end": v(25.95, -47.61) * mm});
            skPoint(sketch, "E88.oppositeSnap0", {"position": v(23.59, -46.53) * mm});
            skLineSegment(sketch, "E88.bottom", {"start": v(27.27, -47.62) * mm, "end": v(29.8, -47.62) * mm});
            skLineSegment(sketch, "E88.top", {"start": v(27.27, -46.53) * mm, "end": v(29.8, -46.53) * mm});
            skLineSegment(sketch, "E88.left", {"start": v(27.27, -47.62) * mm, "end": v(27.27, -46.53) * mm});
            skLineSegment(sketch, "E88.right", {"start": v(29.8, -47.62) * mm, "end": v(29.8, -46.53) * mm});
            skLineSegment(sketch, "E89", {"start": v(26.2, -47.62) * mm, "end": v(27.27, -46.53) * mm});
            skLineSegment(sketch, "E90", {"start": v(30.96, -47.62) * mm, "end": v(29.8, -46.53) * mm});
            skSolve(sketch);
        }
        {
            var Q0;
            Q0 = qSketchRegion(id + "F19", true);
            extrude(context, id + "F20", {"entities" : qUnion([Q0]), "operationType" : NewBodyOperationType.ADD, "depth" : 0.25 * mm});
        }
        {
            var Q0;
            Q0=makeQuery(id+"F20.opExtrude","CAP_FACE",FACE,{"disambiguationData":[OSD([sQuery(id+"F19.wireOp",EDGE,"E84.bottom"),sQuery(id+"F19.wireOp",EDGE,"E84.left"),sQuery(id+"F19.wireOp",EDGE,"E84.right"),sQuery(id+"F19.wireOp",EDGE,"E85.top"),sQuery(id+"F19.wireOp",EDGE,"E86"),sQuery(id+"F19.wireOp",EDGE,"E87")])],"isStart":false});
            var sketch = newSketch(context, id + "F21", { "sketchPlane" : qUnion([Q0])});
            skCircle(sketch, "E91", {"center": v(23.59, -50) * mm, "radius": 2.16 * mm});
            skPoint(sketch, "E91.centerSnap0", {"position": v(25.95, -50) * mm});
            skPoint(sketch, "E91.centerSnap1", {"position": v(23.59, -46.53) * mm});
            skSolve(sketch);
        }
        {
            var Q0;
            Q0 = qSketchRegion(id + "F21", true);
            extrude(context, id + "F22", {"entities" : qUnion([Q0]), "operationType" : NewBodyOperationType.ADD, "depth" : 0.24 * mm});
        }
        {
            var Q0;
            Q0=makeQuery(id+"F20.opExtrude","CAP_FACE",FACE,{"disambiguationData":[OSD([sQuery(id+"F19.wireOp",EDGE,"E83.top"),sQuery(id+"F19.wireOp",EDGE,"E83.left"),sQuery(id+"F19.wireOp",EDGE,"E83.right"),sQuery(id+"F19.wireOp",EDGE,"E88.top"),sQuery(id+"F19.wireOp",EDGE,"E89"),sQuery(id+"F19.wireOp",EDGE,"E90")])],"isStart":false});
            var sketch = newSketch(context, id + "F23", { "sketchPlane" : qUnion([Q0])});
            skCircle(sketch, "E92", {"center": v(28.58, -50) * mm, "radius": 2.16 * mm});
            skPoint(sketch, "E92.centerSnap0", {"position": v(30.96, -50) * mm});
            skPoint(sketch, "E92.centerSnap1", {"position": v(28.58, -52.39) * mm});
            skSolve(sketch);
        }
        {
            var Q0;
            Q0 = qSketchRegion(id + "F23", true);
            extrude(context, id + "F24", {"entities" : qUnion([Q0]), "operationType" : NewBodyOperationType.ADD, "depth" : 0.24 * mm});
        }
        {
            var Q0;
            Q0=makeQuery(id+"F22.opExtrude","CAP_FACE",FACE,{"disambiguationData":[OSD([sQuery(id+"F21.wireOp",EDGE,"E91")])],"isStart":false});
            var sketch = newSketch(context, id + "F25", { "sketchPlane" : qUnion([Q0])});
            skCircle(sketch, "E93", {"center": v(23.59, -50) * mm, "radius": 1.8 * mm});
            skSolve(sketch);
        }
        {
            var Q0;
            Q0 = qSketchRegion(id + "F25", true);
            extrude(context, id + "F26", {"entities" : qUnion([Q0]), "operationType" : NewBodyOperationType.ADD, "depth" : 0.24 * mm});
        }
        {
            var Q0;
            Q0=makeQuery(id+"F24.opExtrude","CAP_FACE",FACE,{"disambiguationData":[OSD([sQuery(id+"F23.wireOp",EDGE,"E92")])],"isStart":false});
            var sketch = newSketch(context, id + "F27", { "sketchPlane" : qUnion([Q0])});
            skCircle(sketch, "E94", {"center": v(28.58, -50) * mm, "radius": 1.8 * mm});
            skSolve(sketch);
        }
        {
            var Q0;
            Q0 = qSketchRegion(id + "F27", true);
            extrude(context, id + "F28", {"entities" : qUnion([Q0]), "operationType" : NewBodyOperationType.ADD, "depth" : 0.24 * mm});
        }
        {
            var Q0;
            Q0=makeQuery(id+"F26.opExtrude","CAP_FACE",FACE,{"disambiguationData":[OSD([sQuery(id+"F25.wireOp",EDGE,"E93")])],"isStart":false});
            var sketch = newSketch(context, id + "F29", { "sketchPlane" : qUnion([Q0])});
            skCircle(sketch, "E95", {"center": v(23.59, -50) * mm, "radius": 2.17 * mm});
            skSolve(sketch);
        }
        {
            var Q0;
            Q0 = qSketchRegion(id + "F29", true);
            extrude(context, id + "F30", {"entities" : qUnion([Q0]), "operationType" : NewBodyOperationType.ADD, "depth" : 5.33 * mm});
        }
        {
            var Q0;
            Q0=makeQuery(id+"F28.opExtrude","CAP_FACE",FACE,{"disambiguationData":[OSD([sQuery(id+"F27.wireOp",EDGE,"E94")])],"isStart":false});
            var sketch = newSketch(context, id + "F31", { "sketchPlane" : qUnion([Q0])});
            skCircle(sketch, "E96", {"center": v(28.58, -50) * mm, "radius": 2.17 * mm});
            skSolve(sketch);
        }
        {
            var Q0;
            Q0 = qSketchRegion(id + "F31", true);
            extrude(context, id + "F32", {"entities" : qUnion([Q0]), "operationType" : NewBodyOperationType.ADD, "depth" : 5.33 * mm});
        }
        {
            var Q0;
            Q0=makeQuery(id+"F30.opExtrude","CAP_EDGE",EDGE,{"disambiguationData":[OSD([sQuery(id+"F29.wireOp",EDGE,"E95")])],"isStart":false});
            var Q1;
            Q1=makeQuery(id+"F32.opExtrude","CAP_EDGE",EDGE,{"disambiguationData":[OSD([sQuery(id+"F31.wireOp",EDGE,"E96")])],"isStart":false});
            fillet(context, id + "F33", {"entities" : qUnion([Q0, Q1]), "radius" : 0.18 * mm, "tangentPropagation" : true, "allowEdgeOverflow" : false});
        }
        {
            var Q0;
            {var subQ0=sQuery(id+"F0.wireOp",EDGE,"E0.left");var subQ1=sQuery(id+"F0.wireOp",EDGE,"E2");var subQ2=sQuery(id+"F0.wireOp",EDGE,"E0.top");var subQ3=sQuery(id+"F0.wireOp",EDGE,"E9");var subQ4=sQuery(id+"F0.wireOp",EDGE,"E8");var subQ5=sQuery(id+"F0.wireOp",EDGE,"E7");var subQ6=sQuery(id+"F0.wireOp",EDGE,"E0.right");var subQ7=sQuery(id+"F0.wireOp",EDGE,"E0.bottom");var subQ8=sQuery(id+"F0.wireOp",EDGE,"E5");var subQ9=sQuery(id+"F0.wireOp",EDGE,"E1");var subQ10=sQuery(id+"F0.wireOp",EDGE,"E3");var subQ11=sQuery(id+"F0.wireOp",EDGE,"E4");var subQ12=sQuery(id+"F0.wireOp",EDGE,"E6");Q0=makeQuery(id+"F3.boolean.opBoolean","SPLIT",FACE,{"disambiguationData":[TD([makeQuery(id+"F1.opExtrude","SWEPT_FACE",FACE,{"disambiguationData":[OSD([subQ7])]})])],"derivedFrom":makeQuery(id+"F1.opExtrude","CAP_FACE",FACE,{"disambiguationData":[OSD([subQ7,subQ2,subQ0,subQ6,subQ9,subQ1,subQ10,subQ11,subQ8,subQ12,subQ5,subQ4,subQ3])],"isStart":false})});}
            var sketch = newSketch(context, id + "F34", { "sketchPlane" : qUnion([Q0])});
            skCircle(sketch, "E97", {"center": v(68.53, -19.66) * mm, "radius": 0.57 * mm});
            skCircle(sketch, "E98", {"center": v(68.53, -21.05) * mm, "radius": 0.57 * mm});
            skCircle(sketch, "E99", {"center": v(68.53, -22.45) * mm, "radius": 0.57 * mm});
            skCircle(sketch, "E100", {"center": v(67.13, -19.66) * mm, "radius": 0.57 * mm});
            skCircle(sketch, "E101", {"center": v(67.13, -21.05) * mm, "radius": 0.57 * mm});
            skCircle(sketch, "E102", {"center": v(67.13, -22.45) * mm, "radius": 0.57 * mm});
            skSolve(sketch);
        }
        {
            var Q0;
            Q0=makeQuery(id+"F34.imprint","IMPRINT",FACE,{"disambiguationData":[TD([[makeQuery(id+"F34.imprint","IMPRINT",EDGE,{"derivedFrom":sQuery(id+"F34.wireOp",EDGE,"E97")}),1.0]])]});
            var Q1;
            Q1=makeQuery(id+"F34.imprint","IMPRINT",FACE,{"disambiguationData":[TD([[makeQuery(id+"F34.imprint","IMPRINT",EDGE,{"derivedFrom":sQuery(id+"F34.wireOp",EDGE,"E98")}),1.0]])]});
            var Q2;
            Q2=makeQuery(id+"F34.imprint","IMPRINT",FACE,{"disambiguationData":[TD([[makeQuery(id+"F34.imprint","IMPRINT",EDGE,{"derivedFrom":sQuery(id+"F34.wireOp",EDGE,"E99")}),1.0]])]});
            var Q3;
            Q3=makeQuery(id+"F34.imprint","IMPRINT",FACE,{"disambiguationData":[TD([[makeQuery(id+"F34.imprint","IMPRINT",EDGE,{"derivedFrom":sQuery(id+"F34.wireOp",EDGE,"E101")}),1.0]])]});
            var Q4;
            Q4=makeQuery(id+"F34.imprint","IMPRINT",FACE,{"disambiguationData":[TD([[makeQuery(id+"F34.imprint","IMPRINT",EDGE,{"derivedFrom":sQuery(id+"F34.wireOp",EDGE,"E102")}),1.0]])]});
            var Q5;
            Q5=makeQuery(id+"F34.imprint","IMPRINT",FACE,{"disambiguationData":[TD([[makeQuery(id+"F34.imprint","IMPRINT",EDGE,{"derivedFrom":sQuery(id+"F34.wireOp",EDGE,"E100")}),1.0]])]});
            extrude(context, id + "F35", {"entities" : qUnion([Q0, Q1, Q2, Q3, Q4, Q5]), "operationType" : NewBodyOperationType.REMOVE, "oppositeDirection" : true, "depth" : 1.59 * mm});
        }
        {
            var Q0;
            Q0=makeQuery(id+"F1.opExtrude","SWEPT_FACE",FACE,{"disambiguationData":[OSD([sQuery(id+"F0.wireOp",EDGE,"E0.left")])]});
            var sketch = newSketch(context, id + "F36", { "sketchPlane" : qUnion([Q0])});
            skLineSegment(sketch, "E103.bottom", {"start": v(1.59, -51.94) * mm, "end": v(11.11, -51.94) * mm});
            skLineSegment(sketch, "E103.top", {"start": v(1.59, -44) * mm, "end": v(11.11, -44) * mm});
            skLineSegment(sketch, "E103.left", {"start": v(1.59, -51.94) * mm, "end": v(1.59, -44) * mm});
            skLineSegment(sketch, "E103.right", {"start": v(11.11, -51.94) * mm, "end": v(11.11, -44) * mm});
            skSolve(sketch);
        }
        {
            var Q0;
            Q0 = qSketchRegion(id + "F36", true);
            extrude(context, id + "F37", {"entities" : qUnion([Q0]), "operationType" : NewBodyOperationType.ADD, "oppositeDirection" : true, "depth" : 1.59 * mm});
        }
        {
            var Q0;
            Q0=makeQuery(id+"F37.opExtrude","CAP_FACE",FACE,{"disambiguationData":[OSD([sQuery(id+"F36.wireOp",EDGE,"E103.bottom"),sQuery(id+"F36.wireOp",EDGE,"E103.top"),sQuery(id+"F36.wireOp",EDGE,"E103.left"),sQuery(id+"F36.wireOp",EDGE,"E103.right")])],"isStart":false});
            var sketch = newSketch(context, id + "F38", { "sketchPlane" : qUnion([Q0])});
            skLineSegment(sketch, "E104.bottom", {"start": v(-1.59, -51.94) * mm, "end": v(-7.22, -51.94) * mm});
            skLineSegment(sketch, "E104.top", {"start": v(-1.59, -44) * mm, "end": v(-7.22, -44) * mm});
            skLineSegment(sketch, "E104.left", {"start": v(-1.59, -51.94) * mm, "end": v(-1.59, -44) * mm});
            skLineSegment(sketch, "E104.right", {"start": v(-7.22, -51.94) * mm, "end": v(-7.22, -44) * mm});
            skSolve(sketch);
        }
        {
            var Q0;
            Q0 = qSketchRegion(id + "F38", true);
            extrude(context, id + "F39", {"entities" : qUnion([Q0]), "operationType" : NewBodyOperationType.ADD, "depth" : 5 / 406.4 * mm});
        }
        {
            var Q0;
            Q0=makeQuery(id+"F37.opExtrude","CAP_FACE",FACE,{"disambiguationData":[OSD([sQuery(id+"F36.wireOp",EDGE,"E103.bottom"),sQuery(id+"F36.wireOp",EDGE,"E103.top"),sQuery(id+"F36.wireOp",EDGE,"E103.left"),sQuery(id+"F36.wireOp",EDGE,"E103.right")])],"isStart":false});
            var sketch = newSketch(context, id + "F40", { "sketchPlane" : qUnion([Q0])});
            skArc(sketch, "E105", {"start": v(-7.22, -44.87) * mm, "mid": v(-10.36, -48.02) * mm, "end": v(-7.22, -51.17) * mm});
            skSolve(sketch);
        }
        {
            var Q0;
            Q0 = qSketchRegion(id + "F40", true);
            var Q1;
            {var subQ0=sQuery(id+"F40.wireOp",EDGE,"E105");Q1=makeQuery(id+"F40.imprint","IMPRINT",FACE,{"disambiguationData":[TD([[makeQuery(id+"F40.imprint","IMPRINT",EDGE,{"derivedFrom":subQ0}),1.0]])]});}
            extrude(context, id + "F41", {"entities" : qUnion([Q0, Q1]), "operationType" : NewBodyOperationType.ADD, "depth" : 5 / 406.4 * mm});
        }
        {
            var Q0;
            {var subQ0=sQuery(id+"F38.wireOp",EDGE,"E104.right");Q0=makeQuery(id+"F41.boolean.opBoolean","MERGE",FACE,{"derivedFrom":[makeQuery(id+"F39.opExtrude","CAP_FACE",FACE,{"disambiguationData":[OSD([sQuery(id+"F38.wireOp",EDGE,"E104.bottom"),sQuery(id+"F38.wireOp",EDGE,"E104.top"),sQuery(id+"F38.wireOp",EDGE,"E104.left"),subQ0])],"isStart":false}),makeQuery(id+"F41.opExtrude","CAP_FACE",FACE,{"disambiguationData":[OSD([subQ0,sQuery(id+"F40.wireOp",EDGE,"E105")])],"isStart":false})]});}
            var sketch = newSketch(context, id + "F42", { "sketchPlane" : qUnion([Q0])});
            skLineSegment(sketch, "E106.bottom", {"start": v(-7.22, -51.17) * mm, "end": v(-1.59, -51.17) * mm});
            skLineSegment(sketch, "E106.top", {"start": v(-7.22, -44.87) * mm, "end": v(-1.59, -44.87) * mm});
            skLineSegment(sketch, "E106.left", {"start": v(-7.22, -51.17) * mm, "end": v(-7.22, -44.87) * mm});
            skLineSegment(sketch, "E106.right", {"start": v(-1.59, -51.17) * mm, "end": v(-1.59, -44.87) * mm});
            skArc(sketch, "E107", {"start": v(-7.22, -44.87) * mm, "mid": v(-10.37, -48.02) * mm, "end": v(-7.22, -51.17) * mm});
            skSolve(sketch);
        }
        {
            var Q0;
            Q0 = qSketchRegion(id + "F42", true);
            extrude(context, id + "F43", {"entities" : qUnion([Q0]), "operationType" : NewBodyOperationType.ADD, "depth" : 1 / 812.8 * mm});
        }
        {
            var Q0;
            {var subQ0=sQuery(id+"F0.wireOp",EDGE,"E0.left");var subQ1=sQuery(id+"F0.wireOp",EDGE,"E2");var subQ2=sQuery(id+"F0.wireOp",EDGE,"E0.top");var subQ3=sQuery(id+"F0.wireOp",EDGE,"E9");var subQ4=sQuery(id+"F0.wireOp",EDGE,"E8");var subQ5=sQuery(id+"F0.wireOp",EDGE,"E7");var subQ6=sQuery(id+"F0.wireOp",EDGE,"E0.right");var subQ7=sQuery(id+"F0.wireOp",EDGE,"E0.bottom");var subQ8=sQuery(id+"F0.wireOp",EDGE,"E5");var subQ9=sQuery(id+"F0.wireOp",EDGE,"E1");var subQ10=sQuery(id+"F0.wireOp",EDGE,"E3");var subQ11=sQuery(id+"F0.wireOp",EDGE,"E4");var subQ12=sQuery(id+"F0.wireOp",EDGE,"E6");Q0=makeQuery(id+"F3.boolean.opBoolean","SPLIT",FACE,{"disambiguationData":[TD([makeQuery(id+"F1.opExtrude","SWEPT_FACE",FACE,{"disambiguationData":[OSD([subQ7])]})])],"derivedFrom":makeQuery(id+"F1.opExtrude","CAP_FACE",FACE,{"disambiguationData":[OSD([subQ7,subQ2,subQ0,subQ6,subQ9,subQ1,subQ10,subQ11,subQ8,subQ12,subQ5,subQ4,subQ3])],"isStart":false})});}
            var sketch = newSketch(context, id + "F44", { "sketchPlane" : qUnion([Q0])});
            skLineSegment(sketch, "E108.bottom", {"start": v(0, -23.64) * mm, "end": v(2.02, -23.64) * mm});
            skLineSegment(sketch, "E108.top", {"start": v(0, -31.18) * mm, "end": v(2.02, -31.18) * mm});
            skLineSegment(sketch, "E108.left", {"start": v(0, -23.64) * mm, "end": v(0, -31.18) * mm});
            skLineSegment(sketch, "E108.right", {"start": v(2.02, -23.64) * mm, "end": v(2.02, -31.18) * mm});
            skLineSegment(sketch, "E109.bottom", {"start": v(0, -23.64) * mm, "end": v(0.18, -23.64) * mm});
            skLineSegment(sketch, "E109.top", {"start": v(0, -22.99) * mm, "end": v(0.18, -22.99) * mm});
            skLineSegment(sketch, "E109.left", {"start": v(0, -23.64) * mm, "end": v(0, -22.99) * mm});
            skLineSegment(sketch, "E109.right", {"start": v(0.18, -23.64) * mm, "end": v(0.18, -22.99) * mm});
            skLineSegment(sketch, "E110.bottom", {"start": v(2.02, -22.99) * mm, "end": v(1.84, -22.99) * mm});
            skLineSegment(sketch, "E110.top", {"start": v(2.02, -23.64) * mm, "end": v(1.84, -23.64) * mm});
            skLineSegment(sketch, "E110.left", {"start": v(2.02, -22.99) * mm, "end": v(2.02, -23.64) * mm});
            skLineSegment(sketch, "E110.right", {"start": v(1.84, -22.99) * mm, "end": v(1.84, -23.64) * mm});
            skLineSegment(sketch, "E111.bottom", {"start": v(0, -31.18) * mm, "end": v(0.18, -31.18) * mm});
            skLineSegment(sketch, "E111.top", {"start": v(0, -31.84) * mm, "end": v(0.18, -31.84) * mm});
            skLineSegment(sketch, "E111.left", {"start": v(0, -31.18) * mm, "end": v(0, -31.84) * mm});
            skLineSegment(sketch, "E111.right", {"start": v(0.18, -31.18) * mm, "end": v(0.18, -31.84) * mm});
            skLineSegment(sketch, "E112.bottom", {"start": v(2.02, -31.18) * mm, "end": v(1.84, -31.18) * mm});
            skLineSegment(sketch, "E112.top", {"start": v(2.02, -31.84) * mm, "end": v(1.84, -31.84) * mm});
            skLineSegment(sketch, "E112.left", {"start": v(2.02, -31.18) * mm, "end": v(2.02, -31.84) * mm});
            skLineSegment(sketch, "E112.right", {"start": v(1.84, -31.18) * mm, "end": v(1.84, -31.84) * mm});
            skSolve(sketch);
        }
        {
            var Q0;
            Q0 = qSketchRegion(id + "F44", true);
            extrude(context, id + "F45", {"entities" : qUnion([Q0]), "operationType" : NewBodyOperationType.ADD, "depth" : 3 / 406.4 * mm});
        }
        {
            var Q0;
            Q0=makeQuery(id+"F45.opExtrude","CAP_FACE",FACE,{"disambiguationData":[OSD([sQuery(id+"F44.wireOp",EDGE,"E108.bottom"),sQuery(id+"F44.wireOp",EDGE,"E108.top"),sQuery(id+"F44.wireOp",EDGE,"E108.left"),sQuery(id+"F44.wireOp",EDGE,"E108.right"),sQuery(id+"F44.wireOp",EDGE,"E109.top"),sQuery(id+"F44.wireOp",EDGE,"E109.left"),sQuery(id+"F44.wireOp",EDGE,"E109.right"),sQuery(id+"F44.wireOp",EDGE,"E110.bottom"),sQuery(id+"F44.wireOp",EDGE,"E110.left"),sQuery(id+"F44.wireOp",EDGE,"E110.right"),sQuery(id+"F44.wireOp",EDGE,"E111.top"),sQuery(id+"F44.wireOp",EDGE,"E111.left"),sQuery(id+"F44.wireOp",EDGE,"E111.right"),sQuery(id+"F44.wireOp",EDGE,"E112.top"),sQuery(id+"F44.wireOp",EDGE,"E112.left"),sQuery(id+"F44.wireOp",EDGE,"E112.right")])],"isStart":false});
            var sketch = newSketch(context, id + "F46", { "sketchPlane" : qUnion([Q0])});
            skLineSegment(sketch, "E113.bottom", {"start": v(1.54, -24.8) * mm, "end": v(0.53, -24.8) * mm});
            skLineSegment(sketch, "E113.top", {"start": v(1.54, -29.67) * mm, "end": v(0.53, -29.67) * mm});
            skLineSegment(sketch, "E113.left", {"start": v(1.54, -24.8) * mm, "end": v(1.54, -29.67) * mm});
            skLineSegment(sketch, "E113.right", {"start": v(0.53, -24.8) * mm, "end": v(0.53, -29.67) * mm});
            skSolve(sketch);
        }
        {
            var Q0;
            Q0 = qSketchRegion(id + "F46", true);
            extrude(context, id + "F47", {"entities" : qUnion([Q0]), "operationType" : NewBodyOperationType.REMOVE, "oppositeDirection" : true, "depth" : 0.5 * mm});
        }
        {
            var Q0;
            Q0=makeQuery(id+"F47.boolean.opBoolean","COPY",FACE,{"derivedFrom":makeQuery(id+"F47.opExtrude","CAP_FACE",FACE,{"disambiguationData":[OSD([sQuery(id+"F46.wireOp",EDGE,"E113.bottom"),sQuery(id+"F46.wireOp",EDGE,"E113.top"),sQuery(id+"F46.wireOp",EDGE,"E113.left"),sQuery(id+"F46.wireOp",EDGE,"E113.right")])],"isStart":false})});
            var sketch = newSketch(context, id + "F48", { "sketchPlane" : qUnion([Q0])});
            skLineSegment(sketch, "E114.bottom", {"start": v(0.53, -29.67) * mm, "end": v(1.54, -29.67) * mm});
            skLineSegment(sketch, "E114.top", {"start": v(0.53, -28.75) * mm, "end": v(1.54, -28.75) * mm});
            skLineSegment(sketch, "E114.left", {"start": v(0.53, -29.67) * mm, "end": v(0.53, -28.75) * mm});
            skLineSegment(sketch, "E114.right", {"start": v(1.54, -29.67) * mm, "end": v(1.54, -28.75) * mm});
            skSolve(sketch);
        }
        {
            var Q0;
            Q0 = qSketchRegion(id + "F48", true);
            extrude(context, id + "F49", {"entities" : qUnion([Q0]), "operationType" : NewBodyOperationType.ADD, "depth" : 1 / 406.4 * mm});
        }
        {
            var Q0;
            Q0=makeQuery(id+"F22.opExtrude","CAP_EDGE",EDGE,{"disambiguationData":[OSD([sQuery(id+"F21.wireOp",EDGE,"E91")])],"isStart":false});
            var Q1;
            Q1=makeQuery(id+"F30.opExtrude","CAP_EDGE",EDGE,{"disambiguationData":[OSD([sQuery(id+"F29.wireOp",EDGE,"E95")])],"isStart":true});
            var Q2;
            Q2=makeQuery(id+"F32.opExtrude","CAP_EDGE",EDGE,{"disambiguationData":[OSD([sQuery(id+"F31.wireOp",EDGE,"E96")])],"isStart":true});
            var Q3;
            Q3=makeQuery(id+"F24.opExtrude","CAP_EDGE",EDGE,{"disambiguationData":[OSD([sQuery(id+"F23.wireOp",EDGE,"E92")])],"isStart":false});
            fillet(context, id + "F50", {"entities" : qUnion([Q0, Q1, Q2, Q3]), "radius" : 0.25 * mm, "tangentPropagation" : true, "allowEdgeOverflow" : false});
        }
    });
